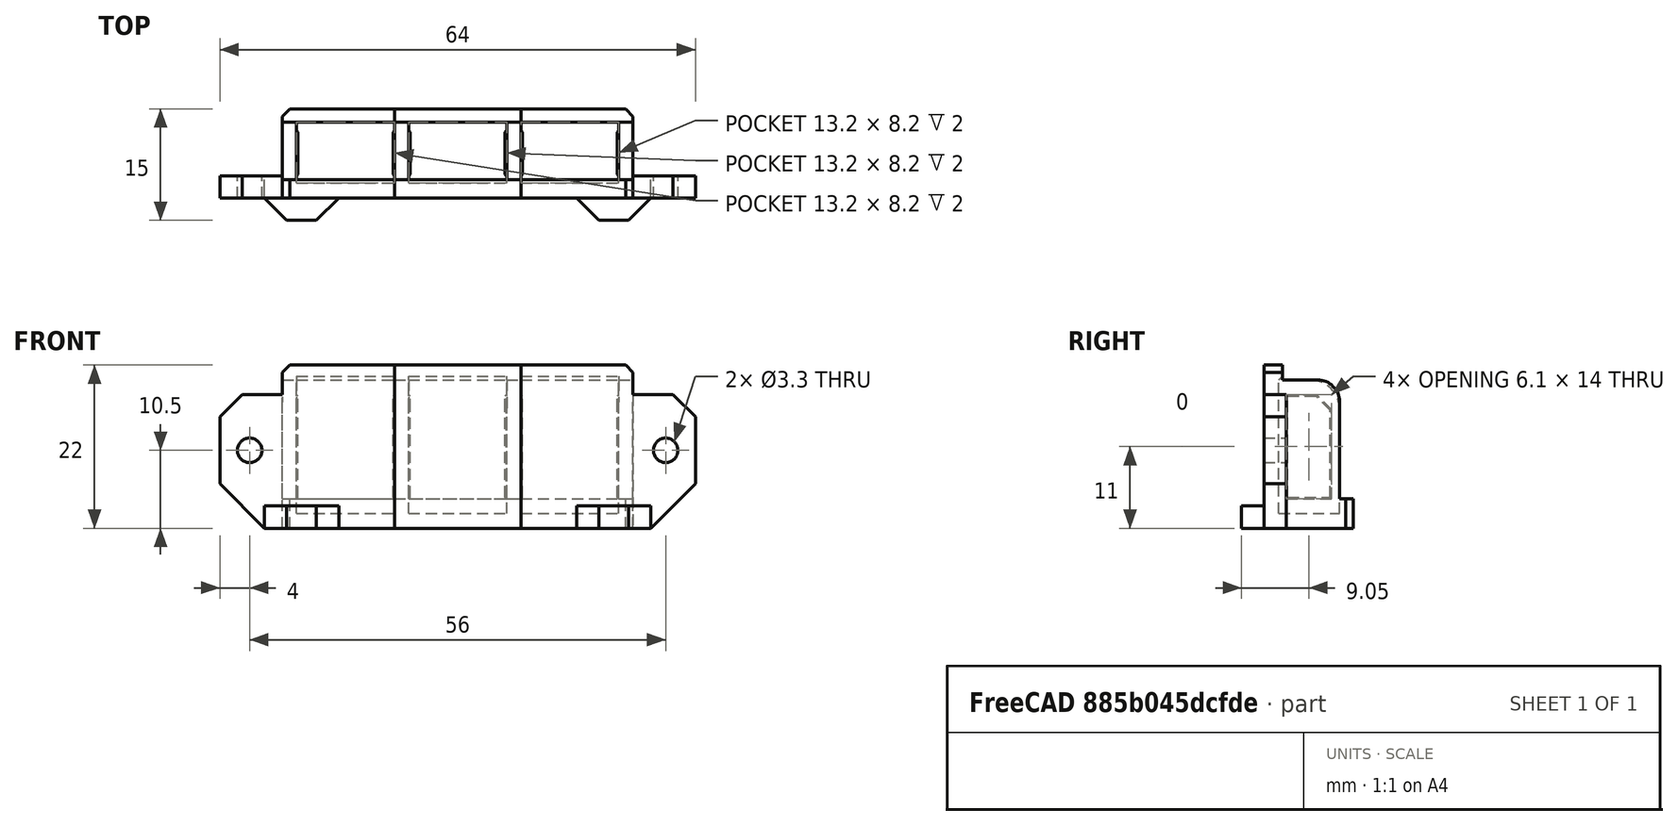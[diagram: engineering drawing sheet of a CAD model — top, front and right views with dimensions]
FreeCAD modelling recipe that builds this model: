
FCSTD DOCUMENT  (FreeCAD 0.18R16146 (Git))
Label: wago-mounter
License: All rights reserved
LicenseURL: http://en.wikipedia.org/wiki/All_rights_reserved
objects: Part::Box×9, Part::Chamfer×8, Part::Feature×5, Part::MultiFuse×5, Part::Cut×4, Part::Cylinder×2, Part::Fillet×1
note: 34 computed .brp shape members not serialized (recipe doc carries the construction recipe); baked Part::Feature solids carry a one-line shape summary decoded from their .brp

FEATURE [Part::Box] Box  label="Cube"
  AttacherType = Attacher::AttachEngine3D
  Height = 18
  Length = 13.2
  Placement = pos=(-6.6,0,2) rot=(0,0,1;0rad)
  Width = 8.2
FEATURE [Part::Box] Box001  label="Cube001"
  AttacherType = Attacher::AttachEngine3D
  Height = 20
  Length = 17
  Placement = pos=(-8.5,-2,0) rot=(0,0,1;0rad)
  Width = 12
FEATURE [Part::Box] Box002  label="Cube002"
  AttacherType = Attacher::AttachEngine3D
  Height = 18
  Length = 17
  Placement = pos=(-8.5,8.2,4) rot=(0,0,1;0rad)
  Width = 8.1
FEATURE [Part::Box] Box003  label="Cube003"
  AttacherType = Attacher::AttachEngine3D
  Height = 14
  Length = 0.2
  Placement = pos=(-6.5,1,4) rot=(0,0,1;0rad)
  Width = 6.1
FEATURE [Part::Chamfer] Chamfer
  Base = -> Box003
  Edges = 1 edges r=2: [Edge12]
FEATURE [Part::Feature] Chamfer001
  Placement = pos=(12.8,0,0) rot=(0,0,1;0rad)
  shape: bbox 0.2 x 6.1 x 14 mm, 7 faces (baked)
FEATURE [Part::Chamfer] Chamfer002
  Base = -> Chamfer
  Edges = 5 edges r=0.19: [Edge8,Edge10,Edge12,Edge13,Edge15]
  Placement = pos=(-0.1,0,0) rot=(0,0,1;0rad)
FEATURE [Part::Chamfer] Chamfer003
  Base = -> Chamfer001
  Edges = 5 edges r=0.19: [Edge1,Edge2,Edge3,Edge4,Edge5]
  Placement = pos=(0.1,0,0) rot=(0,0,1;0rad)
FEATURE [Part::Cut] Cut
  Base = -> Box001
  Tool = -> Box
FEATURE [Part::Cut] Cut001
  Base = -> Cut
  Tool = -> Box002
FEATURE [Part::Box] Box004  label="Cube004"
  AttacherType = Attacher::AttachEngine3D
  Height = 2
  Length = 17
  Placement = pos=(-8.5,-2,20) rot=(0,0,1;0rad)
  Width = 2.5
FEATURE [Part::Box] Box005  label="Cube005"
  AttacherType = Attacher::AttachEngine3D
  Height = 2
  Length = 13.2
  Placement = pos=(-6.6,1.5,20) rot=(0,0,1;0rad)
  Width = 2.5
FEATURE [Part::Chamfer] Chamfer004
  Base = -> Box005
  Edges = 1 edges r=0.5: [Edge10]
  Placement = pos=(0,-1.5,-1.5) rot=(0,0,1;0rad)
FEATURE [Part::Cut] Cut002
  Base = -> Box004
  Tool = -> Chamfer004
FEATURE [Part::Fillet] Fillet
  Base = -> Cut001
  Edges = 2 edges r=4: [Edge7,Edge11]
FEATURE [Part::Feature] Fusion001  label="single-222"
  shape: bbox 17 x 12 x 22 mm, 42 faces (baked)
FEATURE [Part::Feature] Fusion002  label="single-223"
  Placement = pos=(-15.1,0,0) rot=(0,0,1;0rad)
  shape: bbox 17 x 12 x 22 mm, 42 faces (baked)
FEATURE [Part::Feature] Fusion003  label="single-224"
  Placement = pos=(15.1,0,0) rot=(0,0,1;0rad)
  shape: bbox 17 x 12 x 22 mm, 42 faces (baked)
FEATURE [Part::MultiFuse] Fusion004
  Shapes = -> [Fusion002,Fusion003,Fusion001]
FEATURE [Part::Chamfer] Chamfer005
  Base = -> Fusion004
  Edges = 4 edges r=1: [Edge8,Edge11,Edge210,Edge216]
FEATURE [Part::Box] Box006  label="Cube006"
  AttacherType = Attacher::AttachEngine3D
  Height = 18
  Length = 9
  Placement = pos=(-32,-2,0) rot=(0,0,1;0rad)
  Width = 3
FEATURE [Part::Box] Box007  label="Cube007"
  AttacherType = Attacher::AttachEngine3D
  Height = 18
  Length = 9
  Placement = pos=(23,-2,0) rot=(0,0,1;0rad)
  Width = 3
FEATURE [Part::Cylinder] Cylinder
  Angle = 360
  AttacherType = Attacher::AttachEngine3D
  Height = 10
  Placement = pos=(-28,-5.5,10.5) rot=(1,0,0;4.71239rad)
  Radius = 1.65
FEATURE [Part::Cylinder] Cylinder001
  Angle = 360
  AttacherType = Attacher::AttachEngine3D
  Height = 10
  Placement = pos=(28,-5.5,10.5) rot=(-1,0,0;1.5708rad)
  Radius = 1.65
FEATURE [Part::MultiFuse] Fusion007
  Shapes = -> [Cylinder001,Cylinder]
FEATURE [Part::MultiFuse] Fusion006
  Shapes = -> [Box007,Box006,Chamfer005]
FEATURE [Part::Cut] Cut003
  Base = -> Fusion006
  Tool = -> Fusion007
FEATURE [Part::Chamfer] Chamfer006
  Base = -> Cut003
  Edges = 2 edges r=3: [Edge23,Edge268]
FEATURE [Part::Chamfer] Chamfer007
  Base = -> Chamfer006
  Edges = 2 edges r=6: [Edge8,Edge312]
FEATURE [Part::Box] Box008  label="Cube008"
  AttacherType = Attacher::AttachEngine3D
  Height = 3
  Length = 10
  Placement = pos=(-23,-5,0) rot=(0,0,1;0rad)
  Width = 4
FEATURE [Part::Chamfer] Chamfer008
  Base = -> Box008
  Edges = 2 edges r=3: [Edge1,Edge5]
  Placement = pos=(-3,0,0) rot=(0,0,1;0rad)
FEATURE [Part::Feature] Chamfer008001  label="Chamfer009"
  Placement = pos=(39,0,0) rot=(0,0,1;0rad)
  shape: bbox 10 x 4 x 3 mm, 8 faces (baked)
FEATURE [Part::MultiFuse] Fusion008
  Shapes = -> [Chamfer008001,Chamfer007,Chamfer008]
FEATURE [Part::MultiFuse] Fusion  label="single-221"
  Shapes = -> [Chamfer003,Chamfer002,Cut002,Fillet]
